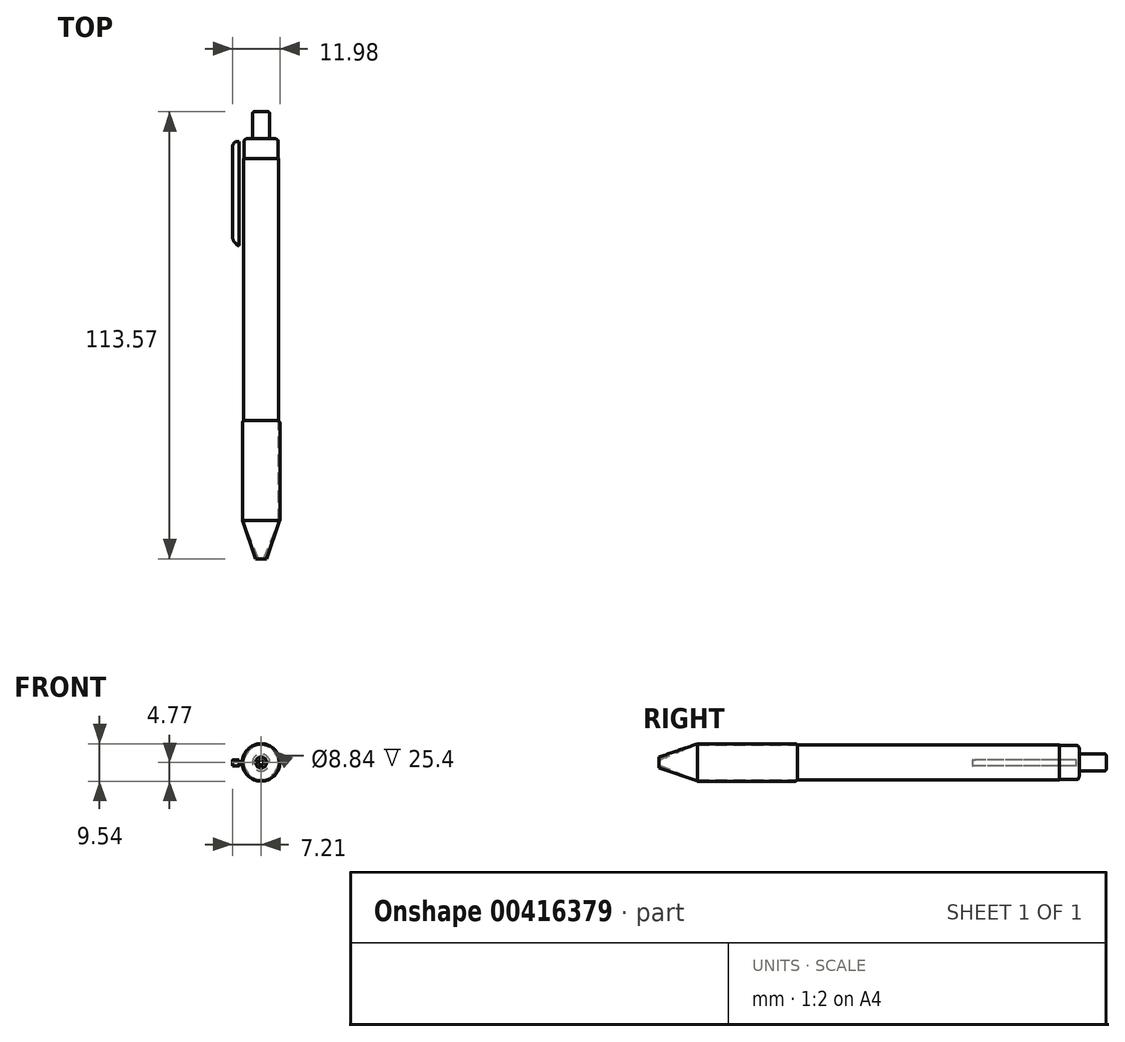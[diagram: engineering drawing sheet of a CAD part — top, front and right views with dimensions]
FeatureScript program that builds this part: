
annotation { "Feature Type Name" : "Feature", "Feature Type Description" : "" }
export const myFeature = defineFeature(function(context is Context, id is Id, definition is map)
    precondition{}
    {
        {
            var Q0;
            Q0=qCreatedBy(makeId("Front.planeOp"),FACE);
            var sketch = newSketch(context, id + "F0", { "sketchPlane" : qUnion([Q0])});
            skCircle(sketch, "E0", {"center": v(0, 0) * mm, "radius": 4.42 * mm});
            skSolve(sketch);
        }
        {
            var Q0;
            Q0=makeQuery(id+"F0.imprint","IMPRINT",FACE,{"disambiguationData":[TD([[makeQuery(id+"F0.imprint","IMPRINT",EDGE,{"derivedFrom":sQuery(id+"F0.wireOp",EDGE,"E0")}),1.0]])]});
            var Q1;
            Q1=sQuery(id+"F0.wireOp",EDGE,"E0");
            extrude(context, id + "F1", {"entities" : qUnion([Q0]), "surfaceEntities" : qUnion([Q1]), "endBound" : BoundingType.SYMMETRIC, "depth" : 66.55 * mm});
        }
        {
            var Q0;
            Q0=makeQuery(id+"F1.opExtrude","CAP_FACE",FACE,{"disambiguationData":[OSD([sQuery(id+"F0.wireOp",EDGE,"E0")])],"isStart":true});
            var sketch = newSketch(context, id + "F2", { "sketchPlane" : qUnion([Q0])});
            skCircle(sketch, "E1", {"center": v(0, 0) * mm, "radius": 4.35 * mm});
            skSolve(sketch);
        }
        {
            var Q0;
            Q0=makeQuery(id+"F2.imprint","IMPRINT",FACE,{"disambiguationData":[TD([[makeQuery(id+"F2.imprint","IMPRINT",EDGE,{"derivedFrom":sQuery(id+"F2.wireOp",EDGE,"E1")}),1.0]])]});
            extrude(context, id + "F3", {"entities" : qUnion([Q0]), "operationType" : NewBodyOperationType.ADD, "depth" : 5.08 * mm});
        }
        {
            var Q0;
            Q0=makeQuery(id+"F3.opExtrude","CAP_FACE",FACE,{"disambiguationData":[OSD([sQuery(id+"F2.wireOp",EDGE,"E1")])],"isStart":false});
            var sketch = newSketch(context, id + "F4", { "sketchPlane" : qUnion([Q0])});
            skCircle(sketch, "E2", {"center": v(0, 0) * mm, "radius": 2.2 * mm});
            skSolve(sketch);
        }
        {
            var Q0;
            Q0=makeQuery(id+"F4.imprint","IMPRINT",FACE,{"disambiguationData":[TD([[makeQuery(id+"F4.imprint","IMPRINT",EDGE,{"derivedFrom":sQuery(id+"F4.wireOp",EDGE,"E2")}),1.0]])]});
            extrude(context, id + "F5", {"entities" : qUnion([Q0]), "operationType" : NewBodyOperationType.ADD, "depth" : 6.86 * mm});
        }
        {
            var Q0;
            Q0=makeQuery(id+"F1.opExtrude","CAP_FACE",FACE,{"disambiguationData":[OSD([sQuery(id+"F0.wireOp",EDGE,"E0")])],"isStart":false});
            var sketch = newSketch(context, id + "F6", { "sketchPlane" : qUnion([Q0])});
            skCircle(sketch, "E3", {"center": v(0, 0) * mm, "radius": 4.77 * mm});
            skSolve(sketch);
        }
        {
            var Q0;
            Q0=makeQuery(id+"F6.imprint","IMPRINT",FACE,{"disambiguationData":[TD([[makeQuery(id+"F6.imprint","IMPRINT",EDGE,{"derivedFrom":sQuery(id+"F6.wireOp",EDGE,"E3")}),1.0]])]});
            extrude(context, id + "F7", {"entities" : qUnion([Q0]), "depth" : 25.4 * mm});
        }
        {
            var Q0;
            Q0=qCreatedBy(makeId("Right.planeOp"),FACE);
            cPlane(context, id + "F8", {"entities" : qUnion([Q0]), "cplaneType" : CPlaneType.OFFSET, "offset" : 4 * mm, "oppositeDirection" : true, "width" : 152.4 * mm, "height" : 152.4 * mm});
        }
        {
            var Q0;
            Q0=qCreatedBy(id+"F8.planeOp",FACE);
            var sketch = newSketch(context, id + "F9", { "sketchPlane" : qUnion([Q0])});
            skLineSegment(sketch, "E4.bottom", {"start": v(37.68, 0.7) * mm, "end": v(35.89, 0.7) * mm});
            skLineSegment(sketch, "E4.top", {"start": v(37.68, -0.91) * mm, "end": v(35.89, -0.91) * mm});
            skLineSegment(sketch, "E4.left", {"start": v(37.68, 0.7) * mm, "end": v(37.68, -0.91) * mm});
            skLineSegment(sketch, "E4.right", {"start": v(35.89, 0.7) * mm, "end": v(35.89, -0.91) * mm});
            skSolve(sketch);
        }
        {
            var Q0;
            Q0=sQuery(id+"F9.wireOp",EDGE,"E4.top");
            var Q1;
            Q1=sQuery(id+"F9.wireOp",EDGE,"E4.left");
            var Q2;
            Q2=sQuery(id+"F9.wireOp",EDGE,"E4.bottom");
            var Q3;
            Q3=sQuery(id+"F9.wireOp",EDGE,"E4.right");
            extrude(context, id + "F10", {"bodyType" : ToolBodyType.SURFACE, "surfaceEntities" : qUnion([Q0, Q1, Q2, Q3]), "oppositeDirection" : true, "depth" : 1.63 * mm});
        }
        {
            var Q0;
            Q0=qCreatedBy(id+"F8.planeOp",FACE);
            var Q1;
            Q1 = qBodyType(qCreatedBy(id + "F12" ,EDGE), BodyType.WIRE);
            cPlane(context, id + "F11", {"entities" : qUnion([Q0, Q1]), "cplaneType" : CPlaneType.OFFSET, "offset" : 1.63 * mm, "oppositeDirection" : true, "width" : 152.4 * mm, "height" : 152.4 * mm});
        }
        {
            var Q0;
            Q0=qCreatedBy(id+"F11.planeOp",FACE);
            var sketch = newSketch(context, id + "F12", { "sketchPlane" : qUnion([Q0])});
            skLineSegment(sketch, "E5.bottom", {"start": v(37.68, -0.91) * mm, "end": v(11.22, -0.91) * mm});
            skLineSegment(sketch, "E5.top", {"start": v(37.68, 0.7) * mm, "end": v(11.22, 0.7) * mm});
            skLineSegment(sketch, "E5.left", {"start": v(37.68, -0.91) * mm, "end": v(37.68, 0.7) * mm});
            skLineSegment(sketch, "E5.right", {"start": v(11.22, -0.91) * mm, "end": v(11.22, 0.7) * mm});
            skSolve(sketch);
        }
        {
            var Q0;
            Q0=makeQuery(id+"F12.imprint","IMPRINT",FACE,{"disambiguationData":[TD([[makeQuery(id+"F12.imprint","IMPRINT",EDGE,{"derivedFrom":sQuery(id+"F12.wireOp",EDGE,"E5.bottom")}),-1.0]])]});
            extrude(context, id + "F13", {"entities" : qUnion([Q0]), "oppositeDirection" : true, "depth" : 1.6 * mm});
        }
        {
            var Q0;
            Q0=qCreatedBy(makeId("Top.planeOp"),FACE);
            var sketch = newSketch(context, id + "F14", { "sketchPlane" : qUnion([Q0])});
            skLineSegment(sketch, "E6", {"start": v(4.72, -58.67) * mm, "end": v(1.4, -68.36) * mm});
            skLineSegment(sketch, "E7", {"start": v(1.4, -68.36) * mm, "end": v(0.62, -68.36) * mm});
            skLineSegment(sketch, "E8", {"start": v(0.62, -68.36) * mm, "end": v(4.72, -58.67) * mm});
            skSolve(sketch);
        }
        {
            var Q0;
            Q0=makeQuery(id+"F14.imprint","IMPRINT",FACE,{"disambiguationData":[TD([[makeQuery(id+"F14.imprint","IMPRINT",EDGE,{"derivedFrom":sQuery(id+"F14.wireOp",EDGE,"E6")}),-1.0]])]});
            var Q1;
            Q1=makeQuery(id+"F7.opExtrude","CAP_EDGE",EDGE,{"disambiguationData":[OSD([sQuery(id+"F6.wireOp",EDGE,"E3")])],"isStart":false});
            revolve(context, id + "F15", {"entities" : qUnion([Q0]), "axis" : qUnion([Q1]), "revolveType" : RevolveType.FULL});
        }
        {
            var Q0;
            Q0=makeQuery(id+"F7.opExtrude","CAP_EDGE",EDGE,{"disambiguationData":[OSD([sQuery(id+"F6.wireOp",EDGE,"E3")])],"isStart":true});
            fillet(context, id + "F16", {"entities" : qUnion([Q0]), "radius" : 0.76 * mm, "tangentPropagation" : true, "allowEdgeOverflow" : false});
        }
        {
            var Q0;
            Q0=makeQuery(id+"F7.opExtrude","CAP_EDGE",EDGE,{"disambiguationData":[OSD([sQuery(id+"F6.wireOp",EDGE,"E3")])],"isStart":false});
            fillet(context, id + "F17", {"entities" : qUnion([Q0]), "radius" : 0.05 * mm, "tangentPropagation" : true, "allowEdgeOverflow" : false});
        }
        {
            var Q0;
            Q0=makeQuery(id+"F5.opExtrude","CAP_EDGE",EDGE,{"disambiguationData":[OSD([sQuery(id+"F4.wireOp",EDGE,"E2")])],"isStart":false});
            fillet(context, id + "F18", {"entities" : qUnion([Q0]), "radius" : 0.5 * mm, "tangentPropagation" : true, "allowEdgeOverflow" : false});
        }
        {
            var Q0;
            Q0=makeQuery(id+"F3.opExtrude","CAP_EDGE",EDGE,{"disambiguationData":[OSD([sQuery(id+"F2.wireOp",EDGE,"E1")])],"isStart":false});
            fillet(context, id + "F19", {"entities" : qUnion([Q0]), "radius" : 0.76 * mm, "tangentPropagation" : true, "allowEdgeOverflow" : false});
        }
        {
            var Q0;
            Q0=makeQuery(id+"F13.opExtrude","CAP_EDGE",EDGE,{"disambiguationData":[OSD([sQuery(id+"F12.wireOp",EDGE,"E5.left")])],"isStart":false});
            fillet(context, id + "F20", {"entities" : qUnion([Q0]), "radius" : 1.27 * mm, "tangentPropagation" : true, "allowEdgeOverflow" : false});
        }
        {
            var Q0;
            Q0=makeQuery(id+"F13.opExtrude","CAP_EDGE",EDGE,{"disambiguationData":[OSD([sQuery(id+"F12.wireOp",EDGE,"E5.right")])],"isStart":false});
            chamfer(context, id + "F21", {"entities" : qUnion([Q0]), "width" : 1.27 * mm, "tangentPropagation" : true});
        }
        {
            var Q0;
            {var subQ0=sQuery(id+"F12.wireOp",EDGE,"E5.right");Q0=makeQuery(id+"F21.opChamfer","BLEND_EDGE",EDGE,{"blendedFrom":[makeQuery(id+"F13.opExtrude","CAP_EDGE",EDGE,{"disambiguationData":[OSD([subQ0])],"isStart":false}),makeQuery(id+"F13.opExtrude","SWEPT_FACE",FACE,{"disambiguationData":[OSD([subQ0])]})],"blendedInto":[makeQuery(id+"F13.opExtrude","SWEPT_FACE",FACE,{"disambiguationData":[OSD([subQ0])]})]});}
            fillet(context, id + "F22", {"entities" : qUnion([Q0]), "radius" : 0.5 * mm, "tangentPropagation" : true, "allowEdgeOverflow" : false});
        }
        {
            var Q0;
            Q0=makeQuery(id+"F13.opExtrude","CAP_EDGE",EDGE,{"disambiguationData":[OSD([sQuery(id+"F12.wireOp",EDGE,"E5.right")])],"isStart":true});
            fillet(context, id + "F23", {"entities" : qUnion([Q0]), "radius" : 0.13 * mm, "tangentPropagation" : true, "allowEdgeOverflow" : false});
        }
        {
            var Q0;
            {var subQ0=sQuery(id+"F12.wireOp",EDGE,"E5.right");Q0=makeQuery(id+"F21.opChamfer","BLEND_EDGE",EDGE,{"blendedFrom":[makeQuery(id+"F13.opExtrude","CAP_EDGE",EDGE,{"disambiguationData":[OSD([subQ0])],"isStart":false}),makeQuery(id+"F13.opExtrude","CAP_FACE",FACE,{"disambiguationData":[OSD([sQuery(id+"F12.wireOp",EDGE,"E5.bottom"),sQuery(id+"F12.wireOp",EDGE,"E5.top"),sQuery(id+"F12.wireOp",EDGE,"E5.left"),subQ0])],"isStart":false})],"blendedInto":[makeQuery(id+"F13.opExtrude","CAP_FACE",FACE,{"disambiguationData":[OSD([sQuery(id+"F12.wireOp",EDGE,"E5.bottom"),sQuery(id+"F12.wireOp",EDGE,"E5.top"),sQuery(id+"F12.wireOp",EDGE,"E5.left"),subQ0])],"isStart":false})]});}
            fillet(context, id + "F24", {"entities" : qUnion([Q0]), "radius" : 1.88 * mm, "tangentPropagation" : true, "allowEdgeOverflow" : false});
        }
    });
